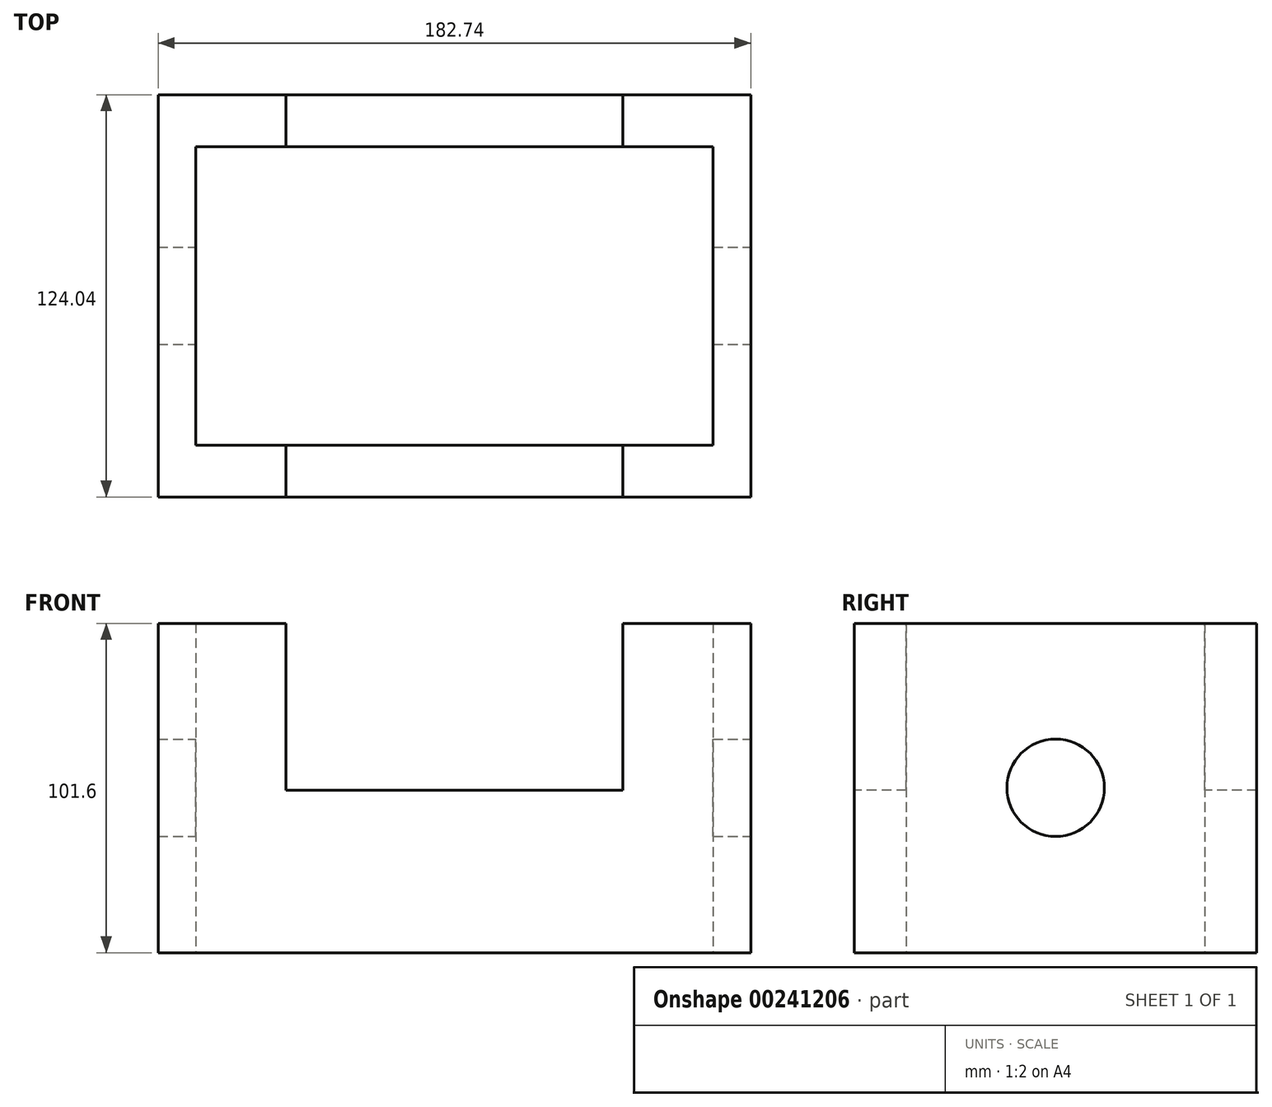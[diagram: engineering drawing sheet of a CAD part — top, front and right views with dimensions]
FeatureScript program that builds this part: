
annotation { "Feature Type Name" : "Feature", "Feature Type Description" : "" }
export const myFeature = defineFeature(function(context is Context, id is Id, definition is map)
    precondition{}
    {
        {
            var Q0;
            Q0=qCreatedBy(makeId("Top.planeOp"),FACE);
            var sketch = newSketch(context, id + "F0", { "sketchPlane" : qUnion([Q0])});
            skLineSegment(sketch, "E0.bottom", {"start": v(91.37, 62.02) * mm, "end": v(-91.37, 62.02) * mm});
            skLineSegment(sketch, "E0.top", {"start": v(91.37, -62.02) * mm, "end": v(-91.37, -62.02) * mm});
            skLineSegment(sketch, "E0.left", {"start": v(91.37, 62.02) * mm, "end": v(91.37, -62.02) * mm});
            skLineSegment(sketch, "E0.right", {"start": v(-91.37, 62.02) * mm, "end": v(-91.37, -62.02) * mm});
            skPoint(sketch, "E0.middle", {"position": v(0, 0) * mm});
            skLineSegment(sketch, "E1.bottom", {"start": v(79.74, 46.04) * mm, "end": v(-79.74, 46.04) * mm});
            skLineSegment(sketch, "E1.top", {"start": v(79.74, -46.04) * mm, "end": v(-79.74, -46.04) * mm});
            skLineSegment(sketch, "E1.left", {"start": v(79.74, 46.04) * mm, "end": v(79.74, -46.04) * mm});
            skLineSegment(sketch, "E1.right", {"start": v(-79.74, 46.04) * mm, "end": v(-79.74, -46.04) * mm});
            skSolve(sketch);
        }
        {
            var Q0;
            Q0=makeQuery(id+"F0.imprint","IMPRINT",FACE,{"disambiguationData":[TD([[makeQuery(id+"F0.imprint","IMPRINT",EDGE,{"derivedFrom":sQuery(id+"F0.wireOp",EDGE,"E0.bottom")}),1.0]])]});
            extrude(context, id + "F1", {"entities" : qUnion([Q0]), "depth" : 101.6 * mm});
        }
        {
            var Q0;
            Q0=makeQuery(id+"F1.opExtrude","SWEPT_FACE",FACE,{"disambiguationData":[OSD([sQuery(id+"F0.wireOp",EDGE,"E0.top")])]});
            var sketch = newSketch(context, id + "F2", { "sketchPlane" : qUnion([Q0])});
            skLineSegment(sketch, "E2.bottom", {"start": v(51.92, 50.13) * mm, "end": v(-51.92, 50.13) * mm});
            skLineSegment(sketch, "E2.top", {"start": v(51.92, 153.07) * mm, "end": v(-51.92, 153.07) * mm});
            skLineSegment(sketch, "E2.left", {"start": v(51.92, 50.13) * mm, "end": v(51.92, 153.07) * mm});
            skLineSegment(sketch, "E2.right", {"start": v(-51.92, 50.13) * mm, "end": v(-51.92, 153.07) * mm});
            skPoint(sketch, "E2.middle", {"position": v(0, 101.6) * mm});
            skSolve(sketch);
        }
        {
            var Q0;
            {var subQ0=sQuery(id+"F2.wireOp",EDGE,"E2.bottom");Q0=makeQuery(id+"F2.imprint","IMPRINT",FACE,{"disambiguationData":[TD([[makeQuery(id+"F2.imprint","IMPRINT",EDGE,{"derivedFrom":subQ0}),-1.0]])]});}
            extrude(context, id + "F3", {"entities" : qUnion([Q0]), "operationType" : NewBodyOperationType.REMOVE, "oppositeDirection" : true, "depth" : 1270 * mm});
        }
        {
            var Q0;
            Q0=makeQuery(id+"F1.opExtrude","SWEPT_FACE",FACE,{"disambiguationData":[OSD([sQuery(id+"F0.wireOp",EDGE,"E0.left")])]});
            var sketch = newSketch(context, id + "F4", { "sketchPlane" : qUnion([Q0])});
            skCircle(sketch, "E3", {"center": v(0, 50.86) * mm, "radius": 15.02 * mm});
            skSolve(sketch);
        }
        {
            var Q0;
            Q0 = qSketchRegion(id + "F4", true);
            extrude(context, id + "F5", {"entities" : qUnion([Q0]), "operationType" : NewBodyOperationType.REMOVE, "oppositeDirection" : true, "depth" : 1270 * mm});
        }
    });
